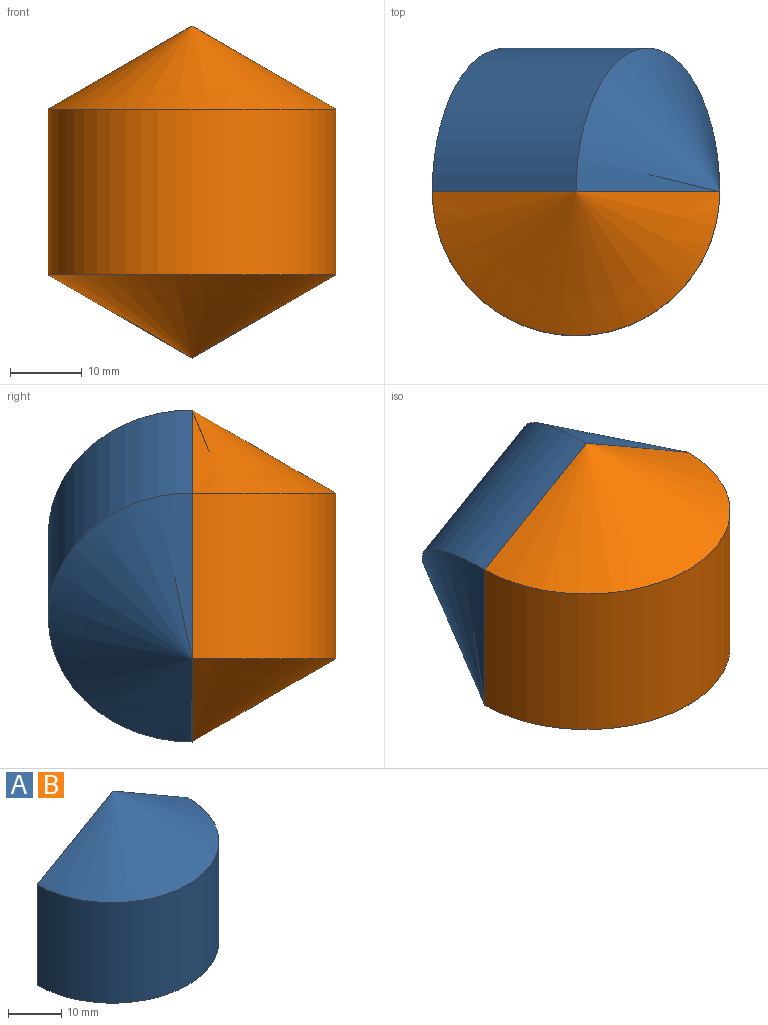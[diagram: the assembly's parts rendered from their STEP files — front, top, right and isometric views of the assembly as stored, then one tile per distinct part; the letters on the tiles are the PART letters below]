
ASSEMBLY  parts=2 mates=1
PART A: 29 faces, bbox 40.1x20.1x46.3 mm
  f0: cylinder r=20mm len=40mm, axis (0,0,1), area 1451mm2, adj f1,f2,f3
  f1: cone r=20mm half-angle=60deg, axis (0,0,-1), area 725.5mm2, adj f0,f3
  f2: cone r=0mm half-angle=60deg, axis (0,0,1), area 725.5mm2, adj f0,f3
  f3: plane 46.19x40mm, normal (0,1,0), area 1178.2mm2, adj f0,f1,f2,f4,f5,f6,f7,f8
  f4: cylinder r=1mm len=6mm, axis (0,1,0), area 25.1mm2, adj f3,f5,f15,f16
  f5: plane 6x5.77mm, normal (0.5,0,-0.87), area 40mm2, adj f3,f4,f6,f17
  f6: cylinder r=1mm len=6mm, axis (0,1,0), area 25.1mm2, adj f3,f5,f7,f18
  f7: plane 6x5.77mm, normal (-0.5,0,-0.87), area 40mm2, adj f3,f6,f8,f19
  f8: cylinder r=1mm len=6mm, axis (0,1,0), area 25.1mm2, adj f3,f7,f9,f20
  f9: plane 6.66x6mm, normal (-1,0,0), area 40mm2, adj f3,f8,f10,f21
  f10: cylinder r=1mm len=6mm, axis (0,1,0), area 25.1mm2, adj f3,f9,f11,f22
  f11: plane 6x5.77mm, normal (-0.5,0,0.87), area 40mm2, adj f3,f10,f12,f23
  f12: cylinder r=1mm len=6mm, axis (0,1,0), area 25.1mm2, adj f3,f11,f13,f24
  f13: plane 6x5.77mm, normal (0.5,0,0.87), area 40mm2, adj f3,f12,f14,f25
  f14: cylinder r=1mm len=6mm, axis (0,1,0), area 25.1mm2, adj f3,f13,f15,f26
  f15: plane 6.66x6mm, normal (1,0,0), area 40mm2, adj f3,f4,f14,f27
  f16: cone r=1mm half-angle=60deg, axis (0,1,0), area 3mm2, adj f4,f17,f27
  f17: plane 7.91x7.11mm, normal (0.25,0.87,-0.43), area 36.7mm2, adj f5,f16,f18,f19,f27,f28
  f18: cone r=1mm half-angle=60deg, axis (0,1,0), area 3mm2, adj f6,f17,f19
  f19: plane 7.83x7.04mm, normal (-0.25,0.87,-0.43), area 36.7mm2, adj f7,f17,f18,f20,f21,f28
  f20: cone r=1mm half-angle=60deg, axis (0,1,0), area 3mm2, adj f8,f19,f21
  f21: plane 8.12x6.93mm, normal (-0.5,0.87,0), area 36.7mm2, adj f9,f19,f20,f22,f23,f28
  f22: cone r=1mm half-angle=60deg, axis (0,1,0), area 3mm2, adj f10,f21,f23
  f23: plane 7.83x7.04mm, normal (-0.25,0.87,0.43), area 36.7mm2, adj f11,f21,f22,f24,f25,f28
  f24: cone r=1mm half-angle=60deg, axis (0,1,0), area 3mm2, adj f12,f23,f25
  f25: plane 7.91x7.11mm, normal (0.25,0.87,0.43), area 36.7mm2, adj f13,f23,f24,f26,f27,f28
  f26: cone r=1mm half-angle=60deg, axis (0,1,0), area 3mm2, adj f14,f25,f27
  f27: plane 8.12x6.93mm, normal (0.5,0.87,0), area 36.7mm2, adj f15,f16,f17,f25,f26,f28
  f28: plane 1.32x1.14mm, normal (0,1,0), area 1.1mm2, adj f17,f19,f21,f23,f25,f27
PART B: same geometry as A
PLACE A rot(axis=(0.87,0,-0.5),180deg) t=(0,0,0)mm
PLACE B at identity
MATE fastened A.f3 <-> B.f3  axis (0,-1,0) through (0,0,0)mm
